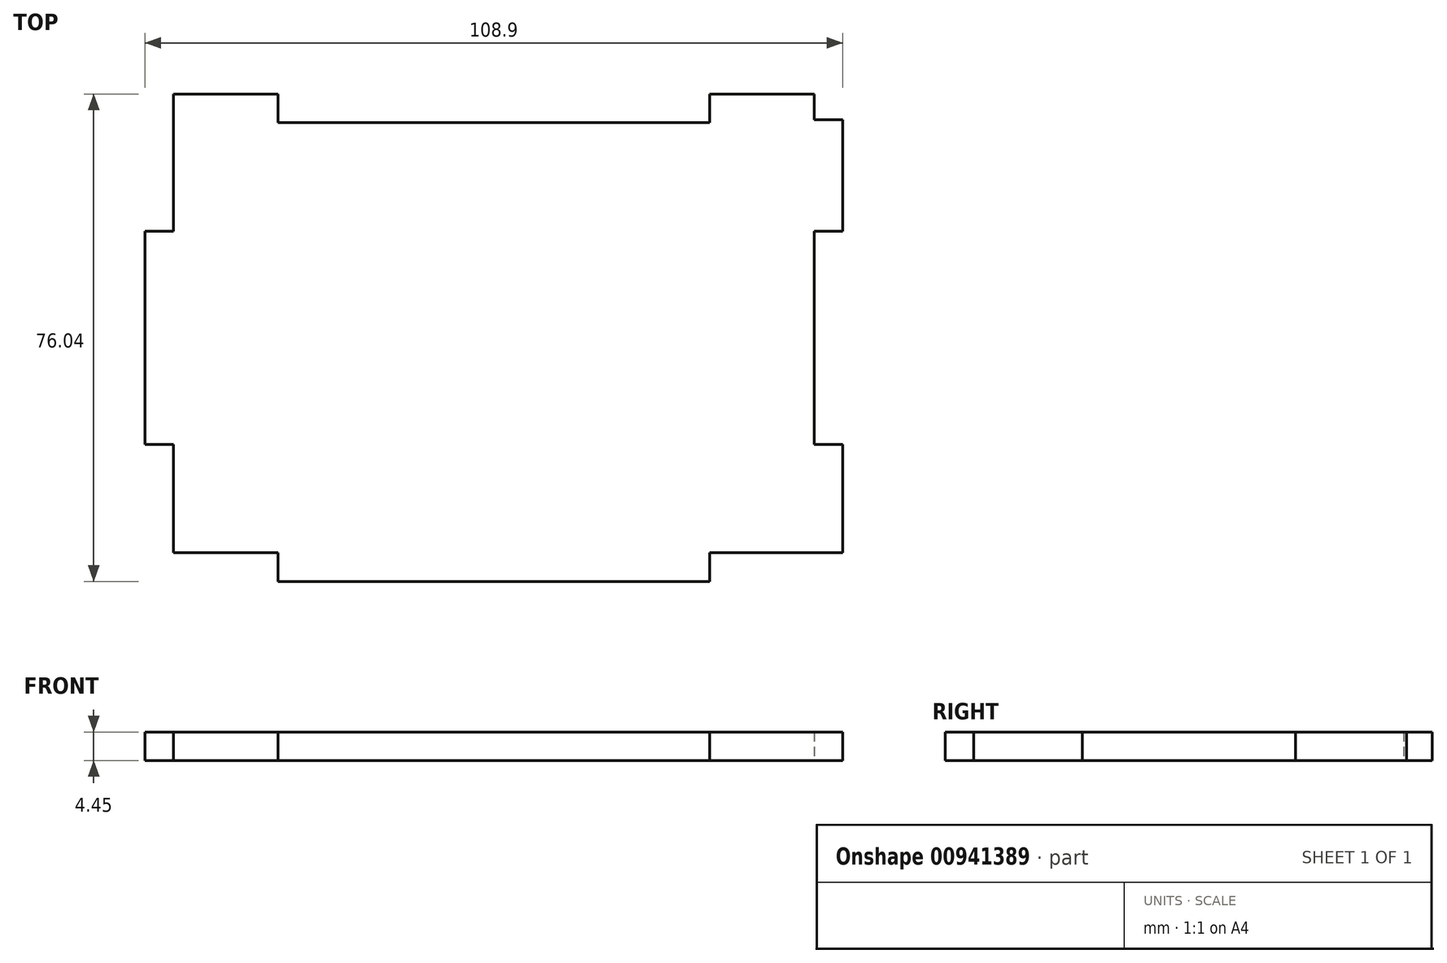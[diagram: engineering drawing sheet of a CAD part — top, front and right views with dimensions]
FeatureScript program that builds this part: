
annotation { "Feature Type Name" : "Feature", "Feature Type Description" : "" }
export const myFeature = defineFeature(function(context is Context, id is Id, definition is map)
    precondition{}
    {
        {
            var Q0;
            Q0=qCreatedBy(makeId("Top.planeOp"),FACE);
            var sketch = newSketch(context, id + "F0", { "sketchPlane" : qUnion([Q0])});
            skLineSegment(sketch, "E0.bottom", {"start": v(50, -33.57) * mm, "end": v(33.7, -33.57) * mm});
            skLineSegment(sketch, "E0.top", {"start": v(33.7, 33.57) * mm, "end": v(-33.7, 33.57) * mm});
            skLineSegment(sketch, "E0.left", {"start": v(50, -16.64) * mm, "end": v(50, 16.64) * mm});
            skLineSegment(sketch, "E0.right", {"start": v(-50, -33.57) * mm, "end": v(-50, -16.64) * mm});
            skPoint(sketch, "E0.middle", {"position": v(0, 0) * mm});
            skLineSegment(sketch, "E1.top", {"start": v(-50, 38.02) * mm, "end": v(-33.7, 38.02) * mm});
            skLineSegment(sketch, "E1.left", {"start": v(-50, 33.57) * mm, "end": v(-50, 38.02) * mm});
            skLineSegment(sketch, "E1.right", {"start": v(-33.7, 33.57) * mm, "end": v(-33.7, 38.02) * mm});
            skLineSegment(sketch, "E2.MirrorCS", {"start": v(50, 38.02) * mm, "end": v(33.7, 38.02) * mm});
            skLineSegment(sketch, "E3.MirrorCS", {"start": v(33.7, 33.57) * mm, "end": v(33.7, 38.02) * mm});
            skLineSegment(sketch, "E4.MirrorCS", {"start": v(50, 33.57) * mm, "end": v(50, 38.02) * mm});
            skLineSegment(sketch, "E5.top", {"start": v(-33.7, -38.02) * mm, "end": v(33.7, -38.02) * mm});
            skLineSegment(sketch, "E5.left", {"start": v(-33.7, -33.57) * mm, "end": v(-33.7, -38.02) * mm});
            skLineSegment(sketch, "E5.right", {"start": v(33.7, -33.57) * mm, "end": v(33.7, -38.02) * mm});
            skLineSegment(sketch, "E6.bottom", {"start": v(-50, -16.64) * mm, "end": v(-54.45, -16.64) * mm});
            skLineSegment(sketch, "E6.top", {"start": v(-50, 16.64) * mm, "end": v(-54.45, 16.64) * mm});
            skLineSegment(sketch, "E6.right", {"start": v(-54.45, -16.64) * mm, "end": v(-54.45, 16.64) * mm});
            skPoint(sketch, "E6.middle", {"position": v(-50, 0) * mm});
            skPoint(sketch, "E7.orphan", {"position": v(-45.55, 16.64) * mm});
            skPoint(sketch, "E8.orphan", {"position": v(-45.55, -16.64) * mm});
            skLineSegment(sketch, "E9.bottom", {"start": v(50, 16.64) * mm, "end": v(54.45, 16.64) * mm});
            skLineSegment(sketch, "E9.top", {"start": v(50, 34) * mm, "end": v(54.45, 34) * mm});
            skLineSegment(sketch, "E9.left", {"start": v(50, 33.57) * mm, "end": v(50, 34) * mm});
            skLineSegment(sketch, "E9.right", {"start": v(54.45, 16.64) * mm, "end": v(54.45, 34) * mm});
            skLineSegment(sketch, "E10.MirrorCS", {"start": v(54.45, -16.64) * mm, "end": v(54.45, -33.57) * mm});
            skLineSegment(sketch, "E11.MirrorCS", {"start": v(50, -16.64) * mm, "end": v(54.45, -16.64) * mm});
            skLineSegment(sketch, "E12", {"start": v(50, -33.57) * mm, "end": v(54.45, -33.57) * mm});
            skPoint(sketch, "E13.MirrorCS.end.orphan", {"position": v(54.45, -34) * mm});
            skPoint(sketch, "E13.MirrorCS.start.orphan", {"position": v(50, -34) * mm});
            skLineSegment(sketch, "E14.trimOffspring", {"start": v(-33.7, -33.57) * mm, "end": v(-50, -33.57) * mm});
            skLineSegment(sketch, "E15.trimOffspring", {"start": v(-50, 16.64) * mm, "end": v(-50, 33.57) * mm});
            skSolve(sketch);
        }
        {
            var Q0;
            Q0=makeQuery(id+"F0.imprint","IMPRINT",FACE,{"disambiguationData":[TD([[makeQuery(id+"F0.imprint","IMPRINT",EDGE,{"derivedFrom":sQuery(id+"F0.wireOp",EDGE,"E0.bottom")}),-1.0]])]});
            extrude(context, id + "F1", {"entities" : qUnion([Q0]), "depth" : 4.45 * mm, "offsetDistance" : 25 * mm});
        }
    });
